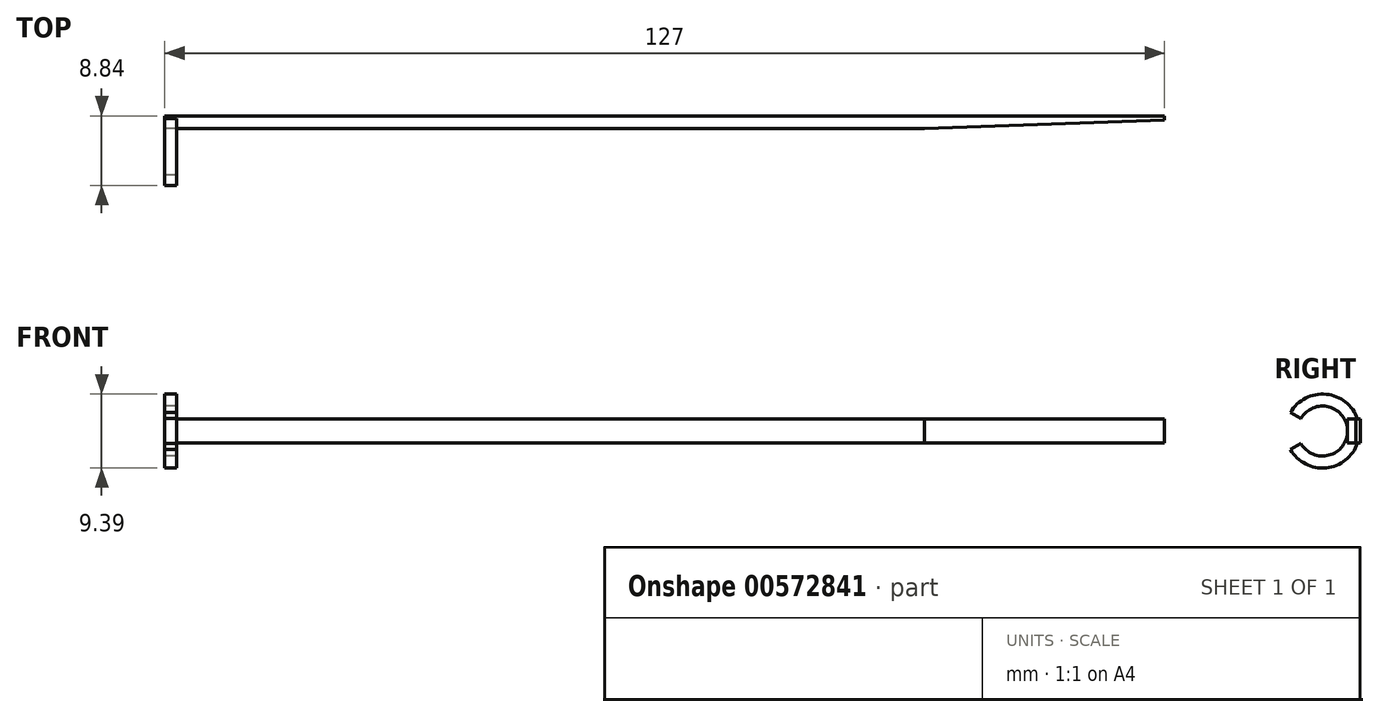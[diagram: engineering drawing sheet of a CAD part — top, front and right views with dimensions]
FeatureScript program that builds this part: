
annotation { "Feature Type Name" : "Feature", "Feature Type Description" : "" }
export const myFeature = defineFeature(function(context is Context, id is Id, definition is map)
    precondition{}
    {
        {
            var Q0;
            Q0=qCreatedBy(makeId("Top.planeOp"),FACE);
            var sketch = newSketch(context, id + "F0", { "sketchPlane" : qUnion([Q0])});
            skLineSegment(sketch, "E0.bottom", {"start": v(-63.5, 0.8) * mm, "end": v(63.48, 0.8) * mm});
            skLineSegment(sketch, "E0.top", {"start": v(-63.5, -0.8) * mm, "end": v(33.02, -0.8) * mm});
            skLineSegment(sketch, "E0.left", {"start": v(-63.5, 0.8) * mm, "end": v(-63.5, -0.8) * mm});
            skPoint(sketch, "E0.middle", {"position": v(0, 0) * mm});
            skLineSegment(sketch, "E1", {"start": v(33.02, -0.8) * mm, "end": v(63.5, 0.25) * mm});
            skLineSegment(sketch, "E2", {"start": v(63.5, 0.25) * mm, "end": v(63.48, 0.8) * mm});
            skSolve(sketch);
        }
        {
            var Q0;
            Q0=makeQuery(id+"F0.imprint","IMPRINT",FACE,{"disambiguationData":[TD([[makeQuery(id+"F0.imprint","IMPRINT",EDGE,{"derivedFrom":sQuery(id+"F0.wireOp",EDGE,"E0.bottom")}),-1.0]])]});
            extrude(context, id + "F1", {"entities" : qUnion([Q0]), "depth" : 3.05 * mm, "offsetDistance" : 25.4 * mm});
        }
        {
            var Q0;
            Q0=makeQuery(id+"F1.opExtrude","SWEPT_FACE",FACE,{"disambiguationData":[OSD([sQuery(id+"F0.wireOp",EDGE,"E0.left")])]});
            var sketch = newSketch(context, id + "F2", { "sketchPlane" : qUnion([Q0])});
            skArc(sketch, "E3", {"start": v(6.72, 3.11) * mm, "mid": v(0.8, 1.52) * mm, "end": v(6.72, -0.06) * mm});
            skArc(sketch, "E4.0", {"start": v(-0.47, 0) * mm, "mid": v(3.52, -3.15) * mm, "end": v(8.04, -0.83) * mm});
            skLineSegment(sketch, "E5", {"start": v(-0.47, 3.05) * mm, "end": v(0.8, 3.05) * mm});
            skLineSegment(sketch, "E6", {"start": v(0.8, 3.05) * mm, "end": v(0.8, 0) * mm});
            skLineSegment(sketch, "E7", {"start": v(0.8, 0) * mm, "end": v(-0.47, 0) * mm});
            skLineSegment(sketch, "E8", {"start": v(6.72, 3.11) * mm, "end": v(8.04, 3.87) * mm});
            skLineSegment(sketch, "E9", {"start": v(8.04, 3.87) * mm, "end": v(6.72, 3.11) * mm});
            skLineSegment(sketch, "E10", {"start": v(6.72, -0.06) * mm, "end": v(8.04, -0.83) * mm});
            skArc(sketch, "E11.trimOffspring", {"start": v(8.04, 3.87) * mm, "mid": v(3.52, 6.2) * mm, "end": v(-0.47, 3.05) * mm});
            skSolve(sketch);
        }
        {
            var Q0;
            {var subQ2=sQuery(id+"F2.wireOp",EDGE,"E5");Q0=makeQuery(id+"F2.imprint","IMPRINT",FACE,{"disambiguationData":[TD([[makeQuery(id+"F2.imprint","IMPRINT",EDGE,{"derivedFrom":subQ2}),1.0]])]});}
            var Q1;
            Q1=makeQuery(id+"F2.imprint","IMPRINT",FACE,{"disambiguationData":[TD([[makeQuery(id+"F2.imprint","IMPRINT",EDGE,{"derivedFrom":sQuery(id+"F2.wireOp",EDGE,"E4.0")}),1.0]])]});
            extrude(context, id + "F3", {"entities" : qUnion([Q0, Q1]), "operationType" : NewBodyOperationType.ADD, "oppositeDirection" : true, "depth" : 1.52 * mm, "offsetDistance" : 25.4 * mm});
        }
    });
